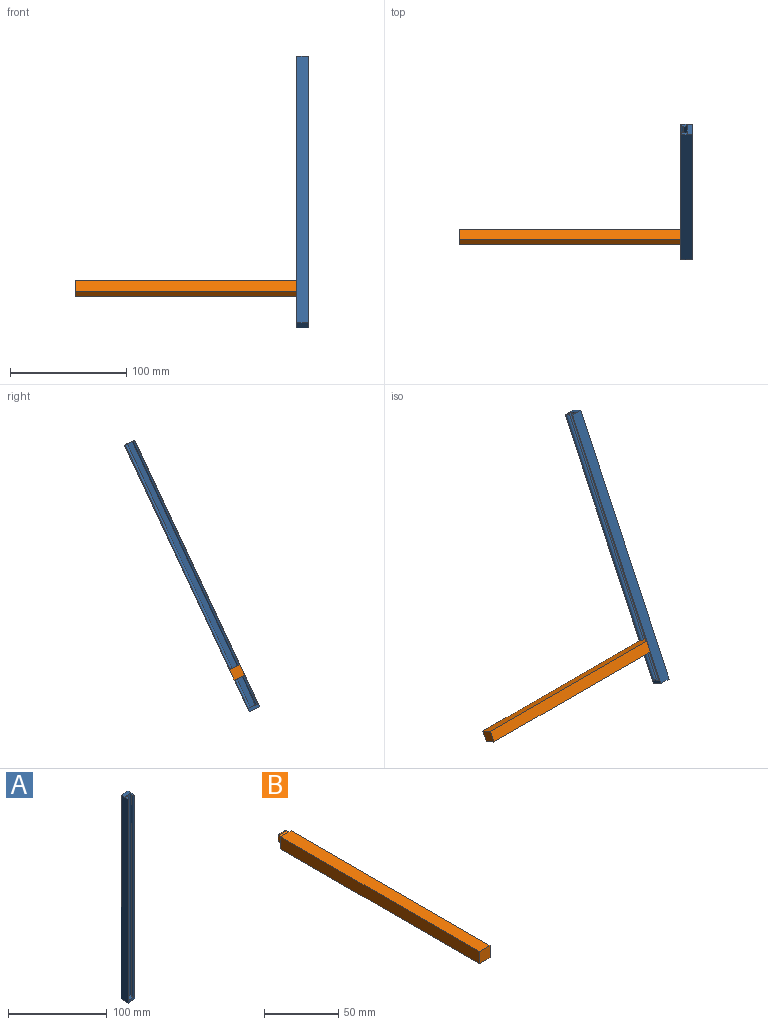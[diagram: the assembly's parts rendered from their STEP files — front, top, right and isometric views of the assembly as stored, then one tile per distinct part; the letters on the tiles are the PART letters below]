
ASSEMBLY  parts=2 mates=1
PART A: 12 faces, bbox 10x10x253 mm
  f0: plane 250x2.79mm, normal (0.93,0.36,0), area 745.7mm2, adj f1,f7,f9,f11
  f1: plane 250x7.2mm, normal (0,-1,0), area 1800mm2, adj f0,f2,f7,f11
  f2: plane 250x2.79mm, normal (-0.93,0.36,0), area 745.7mm2, adj f1,f7,f8,f11
  f3: plane 253x10mm, normal (1,0,0), area 2530mm2, adj f4,f6,f7,f10
  f4: plane 253x10mm, normal (0,1,0), area 2530mm2, adj f3,f5,f7,f10
  f5: plane 253x10mm, normal (-1,0,0), area 2530mm2, adj f4,f6,f7,f10
  f6: plane 253x10mm, normal (0,-1,0), area 327.8mm2, adj f3,f5,f7,f8,f9,f10,f11
  f7: plane 10x10mm, normal (0,0,1), area 68.1mm2, adj f0,f1,f2,f3,f4,f5,f6,f8
  f8: cylinder r=2mm len=250mm, axis (0,0,-1), area 967.8mm2, adj f2,f6,f7,f11
  f9: cylinder r=2mm len=250mm, axis (0,0,-1), area 967.8mm2, adj f0,f6,f7,f11
  f10: plane 10x10mm, normal (0,0,-1), area 100mm2, adj f3,f4,f5,f6
  f11: plane 8.81x5.5mm, normal (0,0,1), area 31.9mm2, adj f0,f1,f2,f6,f8,f9
PART B: 14 faces, bbox 10x195.5x10 mm
  f0: plane 10x10mm, normal (0,1,0), area 49.9mm2, adj f1,f2,f3,f4,f9,f12,f13
  f1: plane 190x10mm, normal (0,0,-1), area 1900mm2, adj f0,f2,f4,f5
  f2: plane 195.5x10mm, normal (1,0,0), area 1928.2mm2, adj f0,f1,f3,f5,f6,f7,f8,f10
  f3: plane 190x10mm, normal (0,0,1), area 1900mm2, adj f0,f2,f4,f5
  f4: plane 190x10mm, normal (-1,0,0), area 1900mm2, adj f0,f1,f3,f5
  f5: plane 10x10mm, normal (0,-1,0), area 100mm2, adj f1,f2,f3,f4
  f6: plane 7x2.11mm, normal (0,-0.36,-0.93), area 15.8mm2, adj f2,f9,f10,f13
  f7: plane 7x4.1mm, normal (0,1,0), area 28.7mm2, adj f2,f9,f10,f11
  f8: plane 7x2.11mm, normal (0,-0.36,0.93), area 15.8mm2, adj f2,f9,f11,f12
  f9: plane 7.16x5.5mm, normal (-1,0,0), area 28.2mm2, adj f0,f6,f7,f8,f10,f11,f12,f13
  f10: cylinder r=1mm len=7mm, axis (-1,0,0), area 13.5mm2, adj f2,f6,f7,f9
  f11: cylinder r=1mm len=7mm, axis (1,0,0), area 13.5mm2, adj f2,f7,f8,f9
  f12: cylinder r=1.5mm len=7mm, axis (1,0,0), area 20.3mm2, adj f0,f2,f8,f9
  f13: cylinder r=1.5mm len=7mm, axis (-1,0,0), area 20.3mm2, adj f0,f2,f6,f9
PLACE A rot(axis=(-0.21,-0.21,-0.95),92.7deg) t=(128.46,-33.73,38.42)mm
PLACE B rot(axis=(-0.64,-0.64,-0.41),135.4deg) t=(128.46,-27.06,76.31)mm
MATE slider A.f11 <-> B.f9  axis (0,0.42,0.91) through (128.46,-38.26,40.54)mm
